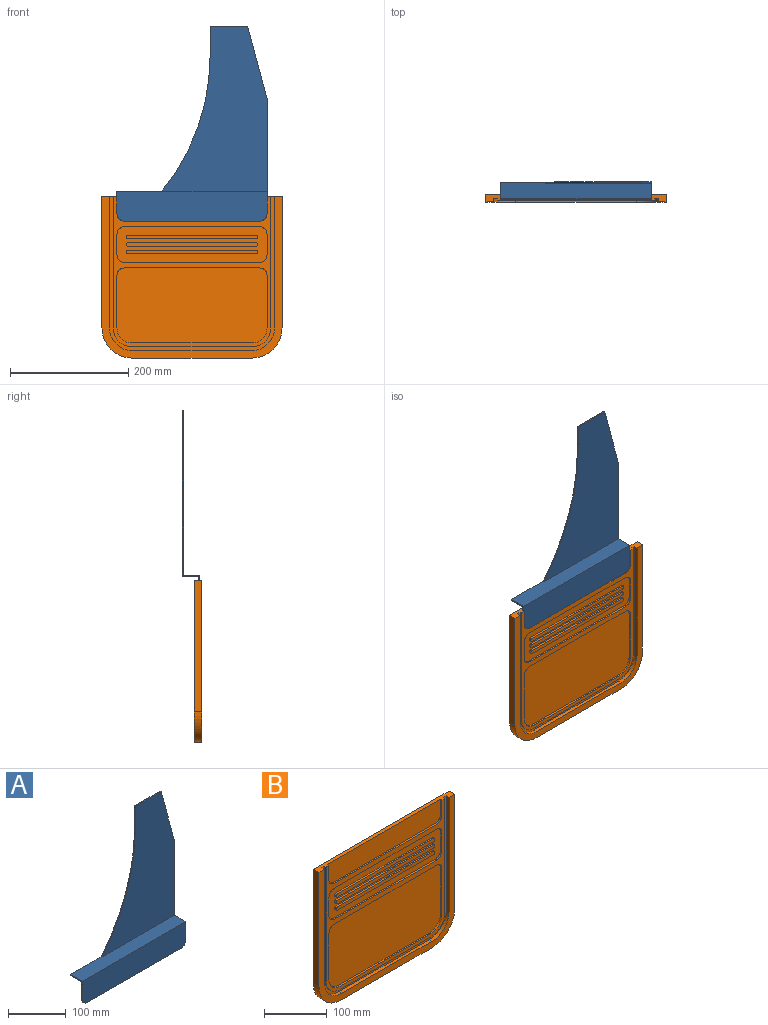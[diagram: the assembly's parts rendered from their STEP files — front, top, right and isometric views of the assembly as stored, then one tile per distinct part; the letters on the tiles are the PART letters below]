
ASSEMBLY  parts=2 mates=1
PART A: 15 faces, bbox 254x29.5x330.2 mm
  f0: plane 254x29.46mm, normal (0,0,1), area 7122.6mm2, adj f1,f3,f4,f8,f11,f12
  f1: plane 194.83x29.46mm, normal (1,0,0), area 451.6mm2, adj f0,f2,f3,f5,f8,f9,f11,f14
  f2: plane 254x27.43mm, normal (0,0,-1), area 6967.7mm2, adj f1,f3,f9,f12
  f3: plane 281.43x254mm, normal (0,1,0), area 31321.3mm2, adj f0,f1,f2,f4,f5,f6,f7,f12
  f4: cylinder r=361.59mm len=228.6mm, axis (0,-1,0), area 502.9mm2, adj f0,f3,f7,f8
  f5: plane 122.67x32.87mm, normal (0.97,0,0.26), area 258.1mm2, adj f1,f3,f6,f8
  f6: plane 63.5x2.03mm, normal (0,0,1), area 129mm2, adj f3,f5,f7,f8
  f7: plane 50.8x2.03mm, normal (-1,0,0), area 103.2mm2, adj f3,f4,f6,f8
  f8: plane 279.4x177.8mm, normal (0,-1,0), area 30805.2mm2, adj f0,f1,f4,f5,f6,f7
  f9: plane 254x48.77mm, normal (0,1,0), area 12317.8mm2, adj f1,f2,f10,f12,f13,f14
  f10: plane 228.6x2.03mm, normal (0,0,-1), area 464.5mm2, adj f9,f11,f13,f14
  f11: plane 254x50.8mm, normal (0,-1,0), area 12834mm2, adj f0,f1,f10,f12,f13,f14
  f12: plane 38.1x29.46mm, normal (-1,0,0), area 133.2mm2, adj f0,f2,f3,f9,f11,f13
  f13: cylinder r=12.7mm len=12.7mm, axis (0,-1,0), area 40.5mm2, adj f9,f10,f11,f12
  f14: cylinder r=12.7mm len=12.7mm, axis (0,1,0), area 40.5mm2, adj f1,f9,f10,f11
PART B: 59 faces, bbox 304.8x12.7x273.1 mm
  f0: plane 279.4x260.35mm, normal (0,-1,0), area 4809.6mm2, adj f3,f7,f8,f15,f16,f17,f18,f29
  f1: plane 254x41.28mm, normal (0,-1,0), area 10414.6mm2, adj f5,f6,f26,f27,f28,f58
  f2: plane 222.25x12.7mm, normal (1,0,0), area 2822.6mm2, adj f4,f12,f14,f58
  f3: plane 222.25x6.35mm, normal (-1,0,0), area 1411.3mm2, adj f0,f4,f15,f58
  f4: plane 304.8x273.05mm, normal (0,-1,0), area 9999.3mm2, adj f2,f3,f10,f11,f13,f14,f15,f16
  f5: plane 28.58x3.18mm, normal (-1,0,0), area 90.7mm2, adj f1,f9,f26,f58
  f6: plane 28.58x3.18mm, normal (1,0,0), area 90.7mm2, adj f1,f9,f28,f58
  f7: plane 222.25x3.18mm, normal (-1,0,0), area 705.6mm2, adj f0,f9,f29,f58
  f8: plane 222.25x3.18mm, normal (1,0,0), area 705.6mm2, adj f0,f9,f31,f58
  f9: plane 266.7x254mm, normal (0,-1,0), area 9798.5mm2, adj f5,f6,f7,f8,f19,f20,f21,f22
  f10: plane 222.25x12.7mm, normal (-1,0,0), area 2822.6mm2, adj f4,f12,f13,f58
  f11: plane 203.2x12.7mm, normal (0,0,-1), area 2580.6mm2, adj f4,f12,f13,f14
  f12: plane 304.8x273.05mm, normal (0,1,0), area 82118mm2, adj f2,f10,f11,f13,f14,f58
  f13: cylinder r=50.8mm len=50.8mm, axis (0,-1,0), area 1013.4mm2, adj f4,f10,f11,f12
  f14: cylinder r=50.8mm len=50.8mm, axis (0,1,0), area 1013.4mm2, adj f2,f4,f11,f12
  f15: cylinder r=38.1mm len=38.1mm, axis (0,1,0), area 380mm2, adj f0,f3,f4,f16
  f16: plane 203.2x6.35mm, normal (0,0,1), area 1290.3mm2, adj f0,f4,f15,f17
  f17: cylinder r=38.1mm len=38.1mm, axis (0,1,0), area 380mm2, adj f0,f4,f16,f18
  f18: plane 222.25x6.35mm, normal (1,0,0), area 1411.3mm2, adj f0,f4,f17,f58
  f19: cylinder r=12.7mm len=12.7mm, axis (0,1,0), area 63.3mm2, adj f9,f20,f40,f42
  f20: plane 228.6x3.18mm, normal (0,0,-1), area 725.8mm2, adj f9,f19,f21,f42
  f21: cylinder r=12.7mm len=12.7mm, axis (0,1,0), area 63.3mm2, adj f9,f20,f22,f42
  f22: plane 88.9x3.18mm, normal (-1,0,0), area 282.3mm2, adj f9,f21,f23,f42
  f23: cylinder r=25.4mm len=25.4mm, axis (0,1,0), area 126.7mm2, adj f9,f22,f24,f42
  f24: plane 203.2x3.18mm, normal (0,0,1), area 645.2mm2, adj f9,f23,f25,f42
  f25: cylinder r=25.4mm len=25.4mm, axis (0,1,0), area 126.7mm2, adj f9,f24,f40,f42
  f26: cylinder r=12.7mm len=12.7mm, axis (0,1,0), area 63.3mm2, adj f1,f5,f9,f27
  f27: plane 228.6x3.18mm, normal (0,0,1), area 725.8mm2, adj f1,f9,f26,f28
  f28: cylinder r=12.7mm len=12.7mm, axis (0,1,0), area 63.3mm2, adj f1,f6,f9,f27
  f29: cylinder r=31.75mm len=31.75mm, axis (0,1,0), area 158.3mm2, adj f0,f7,f9,f30
  f30: plane 203.2x3.18mm, normal (0,0,-1), area 645.2mm2, adj f0,f9,f29,f31
  f31: cylinder r=31.75mm len=31.75mm, axis (0,1,0), area 158.3mm2, adj f0,f8,f9,f30
  f32: cylinder r=12.7mm len=12.7mm, axis (0,1,0), area 63.3mm2, adj f9,f33,f39,f41
  f33: plane 228.6x3.18mm, normal (0,0,-1), area 725.8mm2, adj f9,f32,f34,f41
  f34: cylinder r=12.7mm len=12.7mm, axis (0,1,0), area 63.3mm2, adj f9,f33,f35,f41
  f35: plane 34.93x3.18mm, normal (-1,0,0), area 110.9mm2, adj f9,f34,f36,f41
  f36: cylinder r=12.7mm len=12.7mm, axis (0,1,0), area 63.3mm2, adj f9,f35,f37,f41
  f37: plane 228.6x3.18mm, normal (0,0,1), area 725.8mm2, adj f9,f36,f38,f41
  f38: cylinder r=12.7mm len=12.7mm, axis (0,1,0), area 63.3mm2, adj f9,f37,f39,f41
  f39: plane 34.93x3.18mm, normal (1,0,0), area 110.9mm2, adj f9,f32,f38,f41
  f40: plane 88.9x3.18mm, normal (1,0,0), area 282.3mm2, adj f9,f19,f25,f42
  f41: plane 254x60.33mm, normal (0,-1,0), area 10976.2mm2, adj f32,f33,f34,f35,f36,f37,f38,f39
  f42: plane 254x127mm, normal (0,-1,0), area 31911.9mm2, adj f19,f20,f21,f22,f23,f24,f25,f40
  f43: plane 215.9x3.18mm, normal (0,0,1), area 685.5mm2, adj f41,f44,f46,f47
  f44: cylinder r=3.17mm len=6.35mm, axis (0,1,0), area 31.7mm2, adj f41,f43,f45,f47
  f45: plane 215.9x3.18mm, normal (0,0,-1), area 685.5mm2, adj f41,f44,f46,f47
  f46: cylinder r=3.17mm len=6.35mm, axis (0,1,0), area 31.7mm2, adj f41,f43,f45,f47
  f47: plane 222.25x6.35mm, normal (0,-1,0), area 1402.6mm2, adj f43,f44,f45,f46
  f48: plane 215.9x3.18mm, normal (0,0,1), area 685.5mm2, adj f41,f49,f51,f52
  f49: cylinder r=3.17mm len=6.35mm, axis (0,1,0), area 31.7mm2, adj f41,f48,f50,f52
  f50: plane 215.9x3.18mm, normal (0,0,-1), area 685.5mm2, adj f41,f49,f51,f52
  f51: cylinder r=3.17mm len=6.35mm, axis (0,1,0), area 31.7mm2, adj f41,f48,f50,f52
  f52: plane 222.25x6.35mm, normal (0,-1,0), area 1402.6mm2, adj f48,f49,f50,f51
  f53: plane 215.9x3.18mm, normal (0,0,1), area 685.5mm2, adj f41,f54,f56,f57
  f54: cylinder r=3.17mm len=6.35mm, axis (0,1,0), area 31.7mm2, adj f41,f53,f55,f57
  f55: plane 215.9x3.18mm, normal (0,0,-1), area 685.5mm2, adj f41,f54,f56,f57
  f56: cylinder r=3.17mm len=6.35mm, axis (0,1,0), area 31.7mm2, adj f41,f53,f55,f57
  f57: plane 222.25x6.35mm, normal (0,-1,0), area 1402.6mm2, adj f53,f54,f55,f56
  f58: plane 304.8x12.7mm, normal (0,0,1), area 2137.1mm2, adj f0,f1,f2,f3,f4,f5,f6,f7
PLACE A t=(101.6,19.05,282.58)mm
PLACE B at identity fixed
MATE fastened A.f9 <-> B.f1  axis (0,1,0) through (152.4,-6.35,231.78)mm
